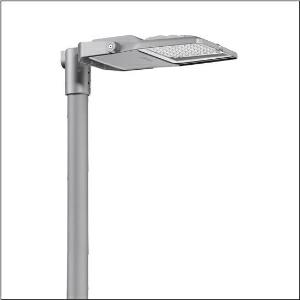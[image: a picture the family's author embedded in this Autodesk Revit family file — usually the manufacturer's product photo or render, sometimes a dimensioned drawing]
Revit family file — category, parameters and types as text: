
# Revit family: floodlight_fl_21_iq_mini___pl64_5xa7772d2e3a_5308
name_source: partatom
category: Lighting Fixtures
units: mm (PartAtom-declared; Revit-internal decimal feet)

## family parameters
Cut with Voids When Loaded = No
Host = Face
Light Source = No
Part Type = Normal
Room Calculation Point = No
Round Connector Dimension = Use Diameter
Shared = No

## types (1)
- --- (1 x LED, 17220 lm, 143 W, 3000K)
    Apparent Load = 143 VA
    CIE Flux Codes = 28 80 98 100 100
    Color Rendering = 70
    Color Temperature = 3000K
    Default Elevation = 1800 mm
    Description = Floodlight FL 21 iQ mini, floodlight, primary light control with lens, of PMMA, primary optical cover: protective disc, of toughened safety glass, transparent, light distribution: PL64, light emission: direct distribution, installation type: surface-mounted, LED, High Power LED, rated luminous flux: 17.220lm, luminous efficacy: 120lm/W, light colour: 730, colour temperature: 3000K, control: Auto-Match, Temp-Guard, Night-Set, Smart-Wire, Desk-Remote (wireless, voltage-free reading and setting of iQ features in the workshop via application-optimized NFC function/RFID function), optimised constant luminous flux control (CLO 2.0), Light-Fading, Lumen-Switch, with terminal, 6-pole, mains connection: 220..240V, AC, 50/60Hz, start of lifetime: 143W, end of service life: 152W, reduction: 61W, luminaire housing, of diecast aluminium, powder-coated, Siteco® metallic grey (DB 702S), corrosivity category C5 mid according to DIN EN ISO 12944, sealing non-destructively replaceable, please order mast flange separately, mast bracket, of steel, galvanised, powder-coated, protection rating (complete): IP66, insulation class (complete): insulation class II (safety insulation), certification: CE, ENEC, VDE, protection symbol: D, impact resistance: IK08, permissible operating ambient temperature: -40..+40°C, permissible operating ambient temperature for outdoor applications: -40..+50°C, standard: DIN EN 12944, LABS conformity tested according to VDMA 24364:2018-05, packaging unit: 1 piece

Light Distribution: PL64
    Height = 70 mm
    Lamp = 1 x LED
    Lamp Light Flux = 17220 lm
    Lamp Power = 143 W
    Lamp count = 1
    Length = 485 mm
    Luminous efficacy = 120 lm/W
    Manufacturer = Siteco
    ModVariant = No
    Model = 5XA7772D2E3A
    Number of Poles = 1
    OnlyDefault = Yes
    Power Factor = 1
    Product Name = Floodlight FL 21 iQ mini | PL64
    Product group = floodlight | pylon annexe
    ProductGroupID = 6200
    Protection Class = Protection class II
    Protection Degree = IP 66
    RLX_Detail_Level = 1
    RLX_Emergency_Light_Flux = 0 lm
    RLX_Emergency_Type = 0
    RLX_Emergency_Type_DB = No
    RlxData = <blob elided: 101493 chars, md5=f4b0bdf2>
    Socket = socket
    Standby Power = 0 W
    System Light Flux = 17220 lm
    System Power = 143 W
    Type Comments = factory setting: luminous flux: 100 % | dim-lin: 254 | 730 mA
    Type Image = l_1007125.jpg
    URL = http://relux.com
    VarID = @adj_115953
    Voltage = 0 V
    Weight = 0.00 kg
    Width = 337 mm

## geometry (parser evidence)
native form markers: Blend x4, Sweep x15
no freeform markers — native parametric forms only
